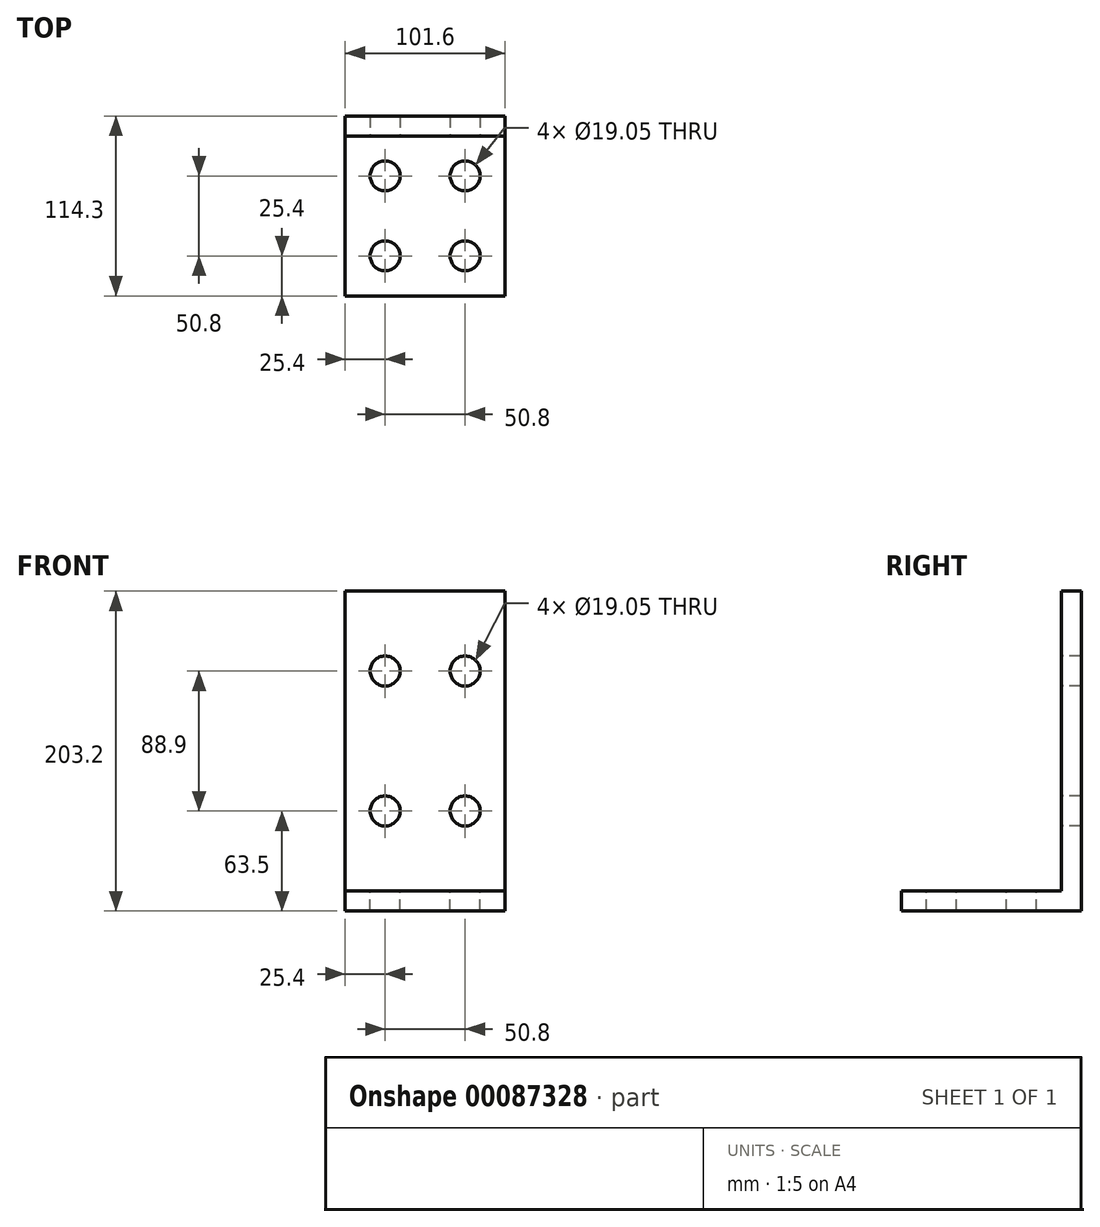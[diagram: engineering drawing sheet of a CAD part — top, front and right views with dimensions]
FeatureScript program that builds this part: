
annotation { "Feature Type Name" : "Feature", "Feature Type Description" : "" }
export const myFeature = defineFeature(function(context is Context, id is Id, definition is map)
    precondition{}
    {
        {
            var Q0;
            Q0=qCreatedBy(makeId("Front.planeOp"),FACE);
            var sketch = newSketch(context, id + "F0", { "sketchPlane" : qUnion([Q0])});
            skLineSegment(sketch, "E0.bottom", {"start": v(0, 0) * mm, "end": v(101.6, 0) * mm});
            skLineSegment(sketch, "E0.top", {"start": v(0, 203.2) * mm, "end": v(101.6, 203.2) * mm});
            skLineSegment(sketch, "E0.left", {"start": v(0, 0) * mm, "end": v(0, 203.2) * mm});
            skLineSegment(sketch, "E0.right", {"start": v(101.6, 0) * mm, "end": v(101.6, 203.2) * mm});
            skSolve(sketch);
        }
        {
            var Q0;
            Q0=qSketchRegion(id+"F0",true);
            extrude(context, id + "F1", {"entities" : qUnion([Q0]), "depth" : 12.7 * mm});
        }
        {
            var Q0;
            Q0=makeQuery(id+"F1.opExtrude","CAP_FACE",FACE,{"disambiguationData":[OSD([sQuery(id+"F0.wireOp",EDGE,"E0.bottom"),sQuery(id+"F0.wireOp",EDGE,"E0.top"),sQuery(id+"F0.wireOp",EDGE,"E0.left"),sQuery(id+"F0.wireOp",EDGE,"E0.right")])],"isStart":false});
            var sketch = newSketch(context, id + "F2", { "sketchPlane" : qUnion([Q0])});
            skLineSegment(sketch, "E1.bottom", {"start": v(0, 0) * mm, "end": v(101.6, 0) * mm});
            skLineSegment(sketch, "E1.top", {"start": v(0, 12.7) * mm, "end": v(101.6, 12.7) * mm});
            skLineSegment(sketch, "E1.left", {"start": v(0, 0) * mm, "end": v(0, 12.7) * mm});
            skLineSegment(sketch, "E1.right", {"start": v(101.6, 0) * mm, "end": v(101.6, 12.7) * mm});
            skSolve(sketch);
        }
        {
            var Q0;
            Q0=qSketchRegion(id+"F2",true);
            extrude(context, id + "F3", {"entities" : qUnion([Q0]), "operationType" : NewBodyOperationType.ADD, "depth" : 101.6 * mm});
        }
        {
            var Q0;
            Q0=makeQuery(id+"F3.opExtrude","SWEPT_FACE",FACE,{"disambiguationData":[OSD([sQuery(id+"F2.wireOp",EDGE,"E1.top")])]});
            var sketch = newSketch(context, id + "F4", { "sketchPlane" : qUnion([Q0])});
            skCircle(sketch, "E2", {"center": v(25.4, -88.9) * mm, "radius": 9.53 * mm});
            skSolve(sketch);
        }
        {
            var Q0;
            Q0=sQuery(id+"F4.wireOp",VERTEX,"E2.center");
            var Q1;
            Q1=makeQuery(id+"F1.opExtrude","SWEPT_BODY",BODY,{"disambiguationData":[OSD([sQuery(id+"F0.wireOp",EDGE,"E0.bottom"),sQuery(id+"F0.wireOp",EDGE,"E0.top"),sQuery(id+"F0.wireOp",EDGE,"E0.left"),sQuery(id+"F0.wireOp",EDGE,"E0.right")])]});
            hole(context, id + "F5", {"style" : HoleStyle.SIMPLE, "endStyle" : HoleEndStyle.BLIND, "holeDiameter" : 19.05 * mm, "holeDepth" : 12.7 * mm, "startFromSketch" : true, "locations" : qUnion([Q0]), "scope" : qUnion([Q1])});
        }
        {
            var Q0;
            Q0=makeQuery(id+"F3.opExtrude","SWEPT_FACE",FACE,{"disambiguationData":[OSD([sQuery(id+"F2.wireOp",EDGE,"E1.top")])]});
            var sketch = newSketch(context, id + "F6", { "sketchPlane" : qUnion([Q0])});
            skCircle(sketch, "E3", {"center": v(25.4, -38.1) * mm, "radius": 9.53 * mm});
            skCircle(sketch, "E4", {"center": v(76.2, -38.1) * mm, "radius": 9.53 * mm});
            skCircle(sketch, "E5", {"center": v(76.2, -88.9) * mm, "radius": 9.53 * mm});
            skSolve(sketch);
        }
        {
            var Q0;
            Q0=sQuery(id+"F6.wireOp",VERTEX,"E3.center");
            var Q1;
            Q1=sQuery(id+"F6.wireOp",VERTEX,"E4.center");
            var Q2;
            Q2=sQuery(id+"F6.wireOp",VERTEX,"E5.center");
            var Q3;
            Q3=makeQuery(id+"F1.opExtrude","SWEPT_BODY",BODY,{"disambiguationData":[OSD([sQuery(id+"F0.wireOp",EDGE,"E0.bottom"),sQuery(id+"F0.wireOp",EDGE,"E0.top"),sQuery(id+"F0.wireOp",EDGE,"E0.left"),sQuery(id+"F0.wireOp",EDGE,"E0.right")])]});
            hole(context, id + "F7", {"style" : HoleStyle.SIMPLE, "endStyle" : HoleEndStyle.BLIND, "holeDiameter" : 19.05 * mm, "holeDepth" : 12.7 * mm, "startFromSketch" : true, "locations" : qUnion([Q0, Q1, Q2]), "scope" : qUnion([Q3])});
        }
        {
            var Q0;
            Q0=makeQuery(id+"F1.opExtrude","CAP_FACE",FACE,{"disambiguationData":[OSD([sQuery(id+"F0.wireOp",EDGE,"E0.bottom"),sQuery(id+"F0.wireOp",EDGE,"E0.top"),sQuery(id+"F0.wireOp",EDGE,"E0.left"),sQuery(id+"F0.wireOp",EDGE,"E0.right")])],"isStart":false});
            var sketch = newSketch(context, id + "F8", { "sketchPlane" : qUnion([Q0])});
            skCircle(sketch, "E6", {"center": v(25.4, 152.4) * mm, "radius": 9.53 * mm});
            skCircle(sketch, "E7", {"center": v(25.4, 63.5) * mm, "radius": 9.53 * mm});
            skCircle(sketch, "E8", {"center": v(76.2, 152.4) * mm, "radius": 9.53 * mm});
            skCircle(sketch, "E9", {"center": v(76.2, 63.5) * mm, "radius": 9.53 * mm});
            skSolve(sketch);
        }
        {
            var Q0;
            Q0=sQuery(id+"F8.wireOp",VERTEX,"E6.center");
            var Q1;
            Q1=sQuery(id+"F8.wireOp",VERTEX,"E8.center");
            var Q2;
            Q2=sQuery(id+"F8.wireOp",VERTEX,"E9.center");
            var Q3;
            Q3=sQuery(id+"F8.wireOp",VERTEX,"E7.center");
            var Q4;
            Q4=makeQuery(id+"F1.opExtrude","SWEPT_BODY",BODY,{"disambiguationData":[OSD([sQuery(id+"F0.wireOp",EDGE,"E0.bottom"),sQuery(id+"F0.wireOp",EDGE,"E0.top"),sQuery(id+"F0.wireOp",EDGE,"E0.left"),sQuery(id+"F0.wireOp",EDGE,"E0.right")])]});
            hole(context, id + "F9", {"style" : HoleStyle.SIMPLE, "endStyle" : HoleEndStyle.BLIND, "holeDiameter" : 19.05 * mm, "holeDepth" : 12.7 * mm, "startFromSketch" : true, "locations" : qUnion([Q0, Q1, Q2, Q3]), "scope" : qUnion([Q4])});
        }
    });
